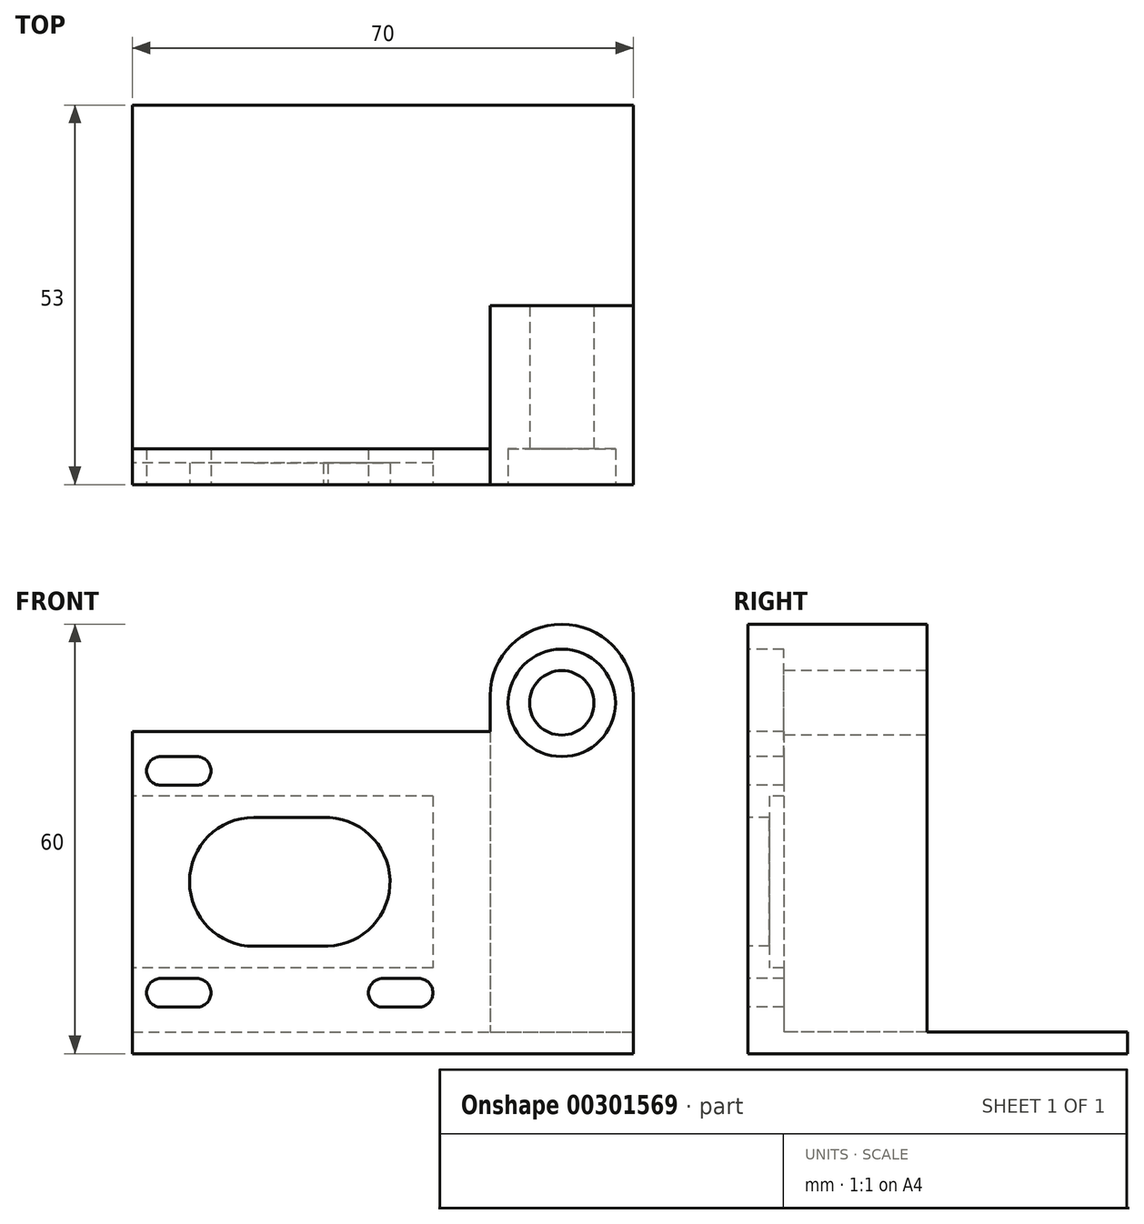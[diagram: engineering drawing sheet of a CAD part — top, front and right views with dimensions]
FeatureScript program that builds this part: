
annotation { "Feature Type Name" : "Feature", "Feature Type Description" : "" }
export const myFeature = defineFeature(function(context is Context, id is Id, definition is map)
    precondition{}
    {
        {
            var Q0;
            Q0=qCreatedBy(makeId("Top.planeOp"),FACE);
            var sketch = newSketch(context, id + "F0", { "sketchPlane" : qUnion([Q0])});
            skLineSegment(sketch, "E0.bottom", {"start": v(-35, 26.5) * mm, "end": v(35, 26.5) * mm});
            skLineSegment(sketch, "E0.top", {"start": v(-35, -26.5) * mm, "end": v(35, -26.5) * mm});
            skLineSegment(sketch, "E0.left", {"start": v(-35, 26.5) * mm, "end": v(-35, -26.5) * mm});
            skLineSegment(sketch, "E0.right", {"start": v(35, 26.5) * mm, "end": v(35, -26.5) * mm});
            skPoint(sketch, "E0.middle", {"position": v(0, 0) * mm});
            skSolve(sketch);
        }
        {
            var Q0;
            Q0=makeQuery(id+"F0.imprint","IMPRINT",FACE,{"disambiguationData":[TD([[makeQuery(id+"F0.imprint","IMPRINT",EDGE,{"derivedFrom":sQuery(id+"F0.wireOp",EDGE,"E0.bottom")}),-1.0]])]});
            extrude(context, id + "F1", {"entities" : qUnion([Q0]), "depth" : 3 * mm});
        }
        {
            var Q0;
            Q0=makeQuery(id+"F1.opExtrude","SWEPT_FACE",FACE,{"disambiguationData":[OSD([sQuery(id+"F0.wireOp",EDGE,"E0.top")])]});
            var sketch = newSketch(context, id + "F2", { "sketchPlane" : qUnion([Q0])});
            skLineSegment(sketch, "E1.bottom", {"start": v(-35, 0) * mm, "end": v(35, 0) * mm});
            skLineSegment(sketch, "E1.top", {"start": v(15, 60) * mm, "end": v(35, 60) * mm});
            skLineSegment(sketch, "E1.left", {"start": v(-35, 0) * mm, "end": v(-35, 45) * mm});
            skLineSegment(sketch, "E1.right", {"start": v(35, 0) * mm, "end": v(35, 60) * mm});
            skLineSegment(sketch, "E2", {"start": v(-35, 45) * mm, "end": v(15, 45) * mm});
            skLineSegment(sketch, "E3", {"start": v(15, 45) * mm, "end": v(15, 60) * mm});
            skSolve(sketch);
        }
        {
            var Q0;
            Q0=qSketchRegion(id+"F2",true);
            extrude(context, id + "F3", {"entities" : qUnion([Q0]), "operationType" : NewBodyOperationType.ADD, "oppositeDirection" : true, "depth" : 5 * mm});
        }
        {
            var Q0;
            Q0=makeQuery(id+"F3.boolean.opBoolean","MERGE",FACE,{"derivedFrom":[makeQuery(id+"F1.opExtrude","SWEPT_FACE",FACE,{"disambiguationData":[OSD([sQuery(id+"F0.wireOp",EDGE,"E0.left")])]}),makeQuery(id+"F3.opExtrude","SWEPT_FACE",FACE,{"disambiguationData":[OSD([sQuery(id+"F2.wireOp",EDGE,"E1.left")])]})]});
            var sketch = newSketch(context, id + "F4", { "sketchPlane" : qUnion([Q0])});
            skLineSegment(sketch, "E4.bottom", {"start": v(21.5, 36) * mm, "end": v(23.5, 36) * mm});
            skLineSegment(sketch, "E4.top", {"start": v(21.5, 12) * mm, "end": v(23.5, 12) * mm});
            skLineSegment(sketch, "E4.left", {"start": v(21.5, 36) * mm, "end": v(21.5, 12) * mm});
            skLineSegment(sketch, "E4.right", {"start": v(23.5, 36) * mm, "end": v(23.5, 12) * mm});
            skSolve(sketch);
        }
        {
            var Q0;
            Q0=makeQuery(id+"F4.imprint","IMPRINT",FACE,{"disambiguationData":[TD([[makeQuery(id+"F4.imprint","IMPRINT",EDGE,{"derivedFrom":sQuery(id+"F4.wireOp",EDGE,"E4.bottom")}),-1.0]])]});
            extrude(context, id + "F5", {"entities" : qUnion([Q0]), "operationType" : NewBodyOperationType.REMOVE, "oppositeDirection" : true, "depth" : 42 * mm});
        }
        {
            var Q0;
            Q0=makeQuery(id+"F3.boolean.opBoolean","MERGE",FACE,{"derivedFrom":[makeQuery(id+"F1.opExtrude","SWEPT_FACE",FACE,{"disambiguationData":[OSD([sQuery(id+"F0.wireOp",EDGE,"E0.top")])]}),makeQuery(id+"F3.opExtrude","CAP_FACE",FACE,{"disambiguationData":[OSD([sQuery(id+"F2.wireOp",EDGE,"E1.bottom"),sQuery(id+"F2.wireOp",EDGE,"E1.top"),sQuery(id+"F2.wireOp",EDGE,"E1.left"),sQuery(id+"F2.wireOp",EDGE,"E1.right")])],"isStart":true})]});
            var sketch = newSketch(context, id + "F6", { "sketchPlane" : qUnion([Q0])});
            skCircle(sketch, "E5", {"center": v(25, 49) * mm, "radius": 4.5 * mm});
            skSolve(sketch);
        }
        {
            var Q0;
            Q0=makeQuery(id+"F6.imprint","IMPRINT",FACE,{"disambiguationData":[TD([[makeQuery(id+"F6.imprint","IMPRINT",EDGE,{"derivedFrom":sQuery(id+"F6.wireOp",EDGE,"E5")}),1.0]])]});
            extrude(context, id + "F7", {"entities" : qUnion([Q0]), "operationType" : NewBodyOperationType.REMOVE, "endBound" : BoundingType.UP_TO_NEXT, "oppositeDirection" : true, "depth" : 25 * mm});
        }
        {
            var Q0;
            Q0=makeQuery(id+"F3.boolean.opBoolean","MERGE",FACE,{"derivedFrom":[makeQuery(id+"F1.opExtrude","SWEPT_FACE",FACE,{"disambiguationData":[OSD([sQuery(id+"F0.wireOp",EDGE,"E0.top")])]}),makeQuery(id+"F3.opExtrude","CAP_FACE",FACE,{"disambiguationData":[OSD([sQuery(id+"F2.wireOp",EDGE,"E1.bottom"),sQuery(id+"F2.wireOp",EDGE,"E1.top"),sQuery(id+"F2.wireOp",EDGE,"E1.left"),sQuery(id+"F2.wireOp",EDGE,"E1.right")])],"isStart":true})]});
            var sketch = newSketch(context, id + "F8", { "sketchPlane" : qUnion([Q0])});
            skLineSegment(sketch, "E6.bottom", {"start": v(-18, 33) * mm, "end": v(-8.32, 33) * mm});
            skLineSegment(sketch, "E6.top", {"start": v(-18, 15) * mm, "end": v(-7.68, 15) * mm});
            skArc(sketch, "E7", {"start": v(-18, 33) * mm, "mid": v(-27, 24) * mm, "end": v(-18, 15) * mm});
            skArc(sketch, "E8", {"start": v(-7.68, 15) * mm, "mid": v(1, 24.32) * mm, "end": v(-8.32, 33) * mm});
            skSolve(sketch);
        }
        {
            var Q0;
            Q0=makeQuery(id+"F8.imprint","IMPRINT",FACE,{"disambiguationData":[TD([[makeQuery(id+"F8.imprint","IMPRINT",EDGE,{"derivedFrom":sQuery(id+"F8.wireOp",EDGE,"E6.bottom")}),-1.0]])]});
            extrude(context, id + "F9", {"entities" : qUnion([Q0]), "operationType" : NewBodyOperationType.REMOVE, "endBound" : BoundingType.UP_TO_NEXT, "oppositeDirection" : true, "depth" : 25 * mm});
        }
        {
            var Q0;
            Q0=makeQuery(id+"F3.boolean.opBoolean","MERGE",FACE,{"derivedFrom":[makeQuery(id+"F1.opExtrude","SWEPT_FACE",FACE,{"disambiguationData":[OSD([sQuery(id+"F0.wireOp",EDGE,"E0.top")])]}),makeQuery(id+"F3.opExtrude","CAP_FACE",FACE,{"disambiguationData":[OSD([sQuery(id+"F2.wireOp",EDGE,"E1.bottom"),sQuery(id+"F2.wireOp",EDGE,"E1.top"),sQuery(id+"F2.wireOp",EDGE,"E1.left"),sQuery(id+"F2.wireOp",EDGE,"E1.right")])],"isStart":true})]});
            var sketch = newSketch(context, id + "F10", { "sketchPlane" : qUnion([Q0])});
            skLineSegment(sketch, "E9.bottom", {"start": v(-31, 10.5) * mm, "end": v(-26, 10.5) * mm});
            skLineSegment(sketch, "E9.top", {"start": v(-31, 6.5) * mm, "end": v(-26, 6.5) * mm});
            skArc(sketch, "E10", {"start": v(-26, 6.5) * mm, "mid": v(-24, 8.5) * mm, "end": v(-26, 10.5) * mm});
            skArc(sketch, "E11", {"start": v(-31, 10.5) * mm, "mid": v(-33, 8.5) * mm, "end": v(-31, 6.5) * mm});
            skLineSegment(sketch, "E12.bottom", {"start": v(-31, 41.5) * mm, "end": v(-26, 41.5) * mm});
            skLineSegment(sketch, "E12.top", {"start": v(-31, 37.5) * mm, "end": v(-26, 37.5) * mm});
            skArc(sketch, "E13", {"start": v(-26, 37.5) * mm, "mid": v(-24, 39.5) * mm, "end": v(-26, 41.5) * mm});
            skArc(sketch, "E14", {"start": v(-31, 41.5) * mm, "mid": v(-33, 39.5) * mm, "end": v(-31, 37.5) * mm});
            skLineSegment(sketch, "E15.bottom", {"start": v(0, 10.5) * mm, "end": v(5, 10.5) * mm});
            skLineSegment(sketch, "E15.top", {"start": v(0, 6.5) * mm, "end": v(5, 6.5) * mm});
            skArc(sketch, "E16", {"start": v(5, 6.5) * mm, "mid": v(7, 8.5) * mm, "end": v(5, 10.5) * mm});
            skArc(sketch, "E17", {"start": v(0, 10.5) * mm, "mid": v(-2, 8.5) * mm, "end": v(0, 6.5) * mm});
            skLineSegment(sketch, "E18", {"start": v(-35, 8.5) * mm, "end": v(6.04, 8.5) * mm, "construction": true});
            skSolve(sketch);
        }
        {
            var Q0;
            Q0=qSketchRegion(id+"F10",true);
            extrude(context, id + "F11", {"entities" : qUnion([Q0]), "operationType" : NewBodyOperationType.REMOVE, "endBound" : BoundingType.UP_TO_NEXT, "oppositeDirection" : true, "depth" : 25 * mm});
        }
        {
            var Q0;
            Q0=makeQuery(id+"F3.opExtrude","CAP_FACE",FACE,{"disambiguationData":[OSD([sQuery(id+"F2.wireOp",EDGE,"E1.bottom"),sQuery(id+"F2.wireOp",EDGE,"E1.top"),sQuery(id+"F2.wireOp",EDGE,"E1.left"),sQuery(id+"F2.wireOp",EDGE,"E1.right")])],"isStart":false});
            var sketch = newSketch(context, id + "F12", { "sketchPlane" : qUnion([Q0])});
            skLineSegment(sketch, "E19.bottom", {"start": v(-35, 60) * mm, "end": v(-15, 60) * mm});
            skLineSegment(sketch, "E19.top", {"start": v(-35, 3) * mm, "end": v(-15, 3) * mm});
            skLineSegment(sketch, "E19.left", {"start": v(-35, 60) * mm, "end": v(-35, 3) * mm});
            skLineSegment(sketch, "E19.right", {"start": v(-15, 60) * mm, "end": v(-15, 3) * mm});
            skSolve(sketch);
        }
        {
            var Q0;
            Q0=makeQuery(id+"F12.imprint","IMPRINT",FACE,{"disambiguationData":[TD([[makeQuery(id+"F12.imprint","IMPRINT",EDGE,{"derivedFrom":sQuery(id+"F12.wireOp",EDGE,"E19.bottom")}),1.0]])]});
            extrude(context, id + "F13", {"entities" : qUnion([Q0]), "operationType" : NewBodyOperationType.ADD, "depth" : 20 * mm});
        }
        {
            var Q0;
            Q0=makeQuery(id+"F3.boolean.opBoolean","MERGE",FACE,{"derivedFrom":[makeQuery(id+"F1.opExtrude","SWEPT_FACE",FACE,{"disambiguationData":[OSD([sQuery(id+"F0.wireOp",EDGE,"E0.top")])]}),makeQuery(id+"F3.opExtrude","CAP_FACE",FACE,{"disambiguationData":[OSD([sQuery(id+"F2.wireOp",EDGE,"E1.bottom"),sQuery(id+"F2.wireOp",EDGE,"E1.top"),sQuery(id+"F2.wireOp",EDGE,"E1.left"),sQuery(id+"F2.wireOp",EDGE,"E1.right")])],"isStart":true})]});
            var sketch = newSketch(context, id + "F14", { "sketchPlane" : qUnion([Q0])});
            skCircle(sketch, "E20", {"center": v(25, 49) * mm, "radius": 7.5 * mm});
            skSolve(sketch);
        }
        {
            var Q0;
            Q0=makeQuery(id+"F14.imprint","IMPRINT",FACE,{"disambiguationData":[TD([[makeQuery(id+"F14.imprint","IMPRINT",EDGE,{"derivedFrom":sQuery(id+"F14.wireOp",EDGE,"E20")}),1.0]])]});
            extrude(context, id + "F15", {"entities" : qUnion([Q0]), "operationType" : NewBodyOperationType.REMOVE, "oppositeDirection" : true, "depth" : 5 * mm});
        }
        {
            var Q0;
            Q0=makeQuery(id+"F13.boolean.opBoolean","MERGE",EDGE,{"derivedFrom":[makeQuery(id+"F3.opExtrude","SWEPT_EDGE",EDGE,{"disambiguationData":[OSD([sQuery(id+"F2.wireOp",EDGE,"E1.top"),sQuery(id+"F2.wireOp",EDGE,"E3")])]}),makeQuery(id+"F13.opExtrude","SWEPT_EDGE",EDGE,{"disambiguationData":[OSD([sQuery(id+"F12.wireOp",EDGE,"E19.bottom"),sQuery(id+"F12.wireOp",EDGE,"E19.right")])]})]});
            var Q1;
            Q1=makeQuery(id+"F13.boolean.opBoolean","MERGE",EDGE,{"derivedFrom":[makeQuery(id+"F3.opExtrude","SWEPT_EDGE",EDGE,{"disambiguationData":[OSD([sQuery(id+"F2.wireOp",EDGE,"E1.top"),sQuery(id+"F2.wireOp",EDGE,"E1.right")])]}),makeQuery(id+"F13.opExtrude","SWEPT_EDGE",EDGE,{"disambiguationData":[OSD([sQuery(id+"F12.wireOp",EDGE,"E19.bottom"),sQuery(id+"F12.wireOp",EDGE,"E19.left")])]})]});
            fillet(context, id + "F16", {"entities" : qUnion([Q0, Q1]), "radius" : 10 * mm, "tangentPropagation" : true, "allowEdgeOverflow" : false});
        }
    });
